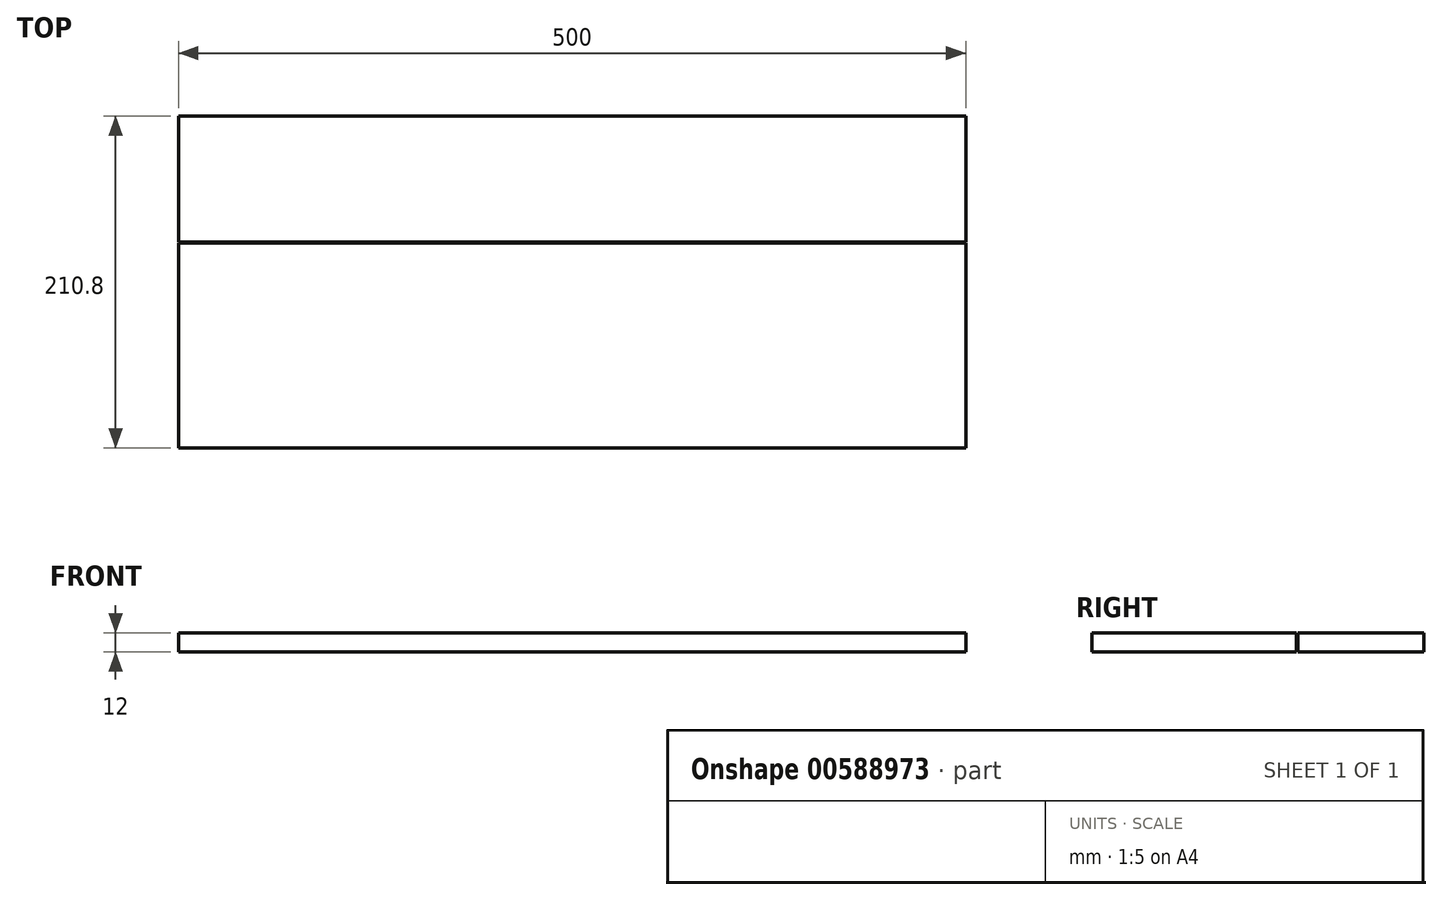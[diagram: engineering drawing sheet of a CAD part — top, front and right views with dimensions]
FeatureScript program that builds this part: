
annotation { "Feature Type Name" : "Feature", "Feature Type Description" : "" }
export const myFeature = defineFeature(function(context is Context, id is Id, definition is map)
    precondition{}
    {
        {
            var Q0;
            Q0=qCreatedBy(makeId("Top.planeOp"),FACE);
            var sketch = newSketch(context, id + "F0", { "sketchPlane" : qUnion([Q0])});
            skLineSegment(sketch, "E0.bottom", {"start": v(0, 0) * mm, "end": v(500, 0) * mm});
            skLineSegment(sketch, "E0.top", {"start": v(0, -130) * mm, "end": v(500, -130) * mm});
            skLineSegment(sketch, "E0.left", {"start": v(0, 0) * mm, "end": v(0, -130) * mm});
            skLineSegment(sketch, "E0.right", {"start": v(500, 0) * mm, "end": v(500, -130) * mm});
            skSolve(sketch);
        }
        {
            var Q0;
            Q0 = qSketchRegion(id + "F0", true);
            extrude(context, id + "F1", {"entities" : qUnion([Q0]), "oppositeDirection" : true, "depth" : 12 * mm, "offsetDistance" : 25 * mm});
        }
        {
            var Q0;
            Q0=qCreatedBy(makeId("Top.planeOp"),FACE);
            var sketch = newSketch(context, id + "F2", { "sketchPlane" : qUnion([Q0])});
            skLineSegment(sketch, "E1.bottom", {"start": v(0, 0) * mm, "end": v(500, 0) * mm});
            skLineSegment(sketch, "E1.top", {"start": v(0, 80) * mm, "end": v(500, 80) * mm});
            skLineSegment(sketch, "E1.left", {"start": v(0, 0) * mm, "end": v(0, 80) * mm});
            skLineSegment(sketch, "E1.right", {"start": v(500, 0) * mm, "end": v(500, 80) * mm});
            skSolve(sketch);
        }
        {
            var Q0;
            Q0=makeQuery(id+"F1.opExtrude","SWEPT_BODY",BODY,{"disambiguationData":[OSD([sQuery(id+"F0.wireOp",EDGE,"E0.bottom"),sQuery(id+"F0.wireOp",EDGE,"E0.top"),sQuery(id+"F0.wireOp",EDGE,"E0.left"),sQuery(id+"F0.wireOp",EDGE,"E0.right")])]});
            transform(context, id + "F3", {"entities" : qUnion([Q0]), "transformType" : TransformType.TRANSLATION_3D, "dx" : 54 * mm, "dy" : -89 * mm, "dz" : 0 * mm, "makeCopy" : false});
        }
        {
            var Q0;
            Q0=makeQuery(id+"F2.imprint","IMPRINT",FACE,{"disambiguationData":[TD([[makeQuery(id+"F2.imprint","IMPRINT",EDGE,{"derivedFrom":sQuery(id+"F2.wireOp",EDGE,"E1.bottom")}),1.0]])]});
            extrude(context, id + "F4", {"entities" : qUnion([Q0]), "oppositeDirection" : true, "depth" : 12 * mm, "offsetDistance" : 25 * mm});
        }
        {
            var Q0;
            Q0=makeQuery(id+"F1.opExtrude","SWEPT_BODY",BODY,{"disambiguationData":[OSD([sQuery(id+"F0.wireOp",EDGE,"E0.bottom"),sQuery(id+"F0.wireOp",EDGE,"E0.top"),sQuery(id+"F0.wireOp",EDGE,"E0.left"),sQuery(id+"F0.wireOp",EDGE,"E0.right")])]});
            transform(context, id + "F5", {"entities" : qUnion([Q0]), "transformType" : TransformType.TRANSLATION_3D, "dx" : -54 * mm, "dy" : 88.2 * mm, "dz" : 0 * mm, "makeCopy" : false});
        }
    });
